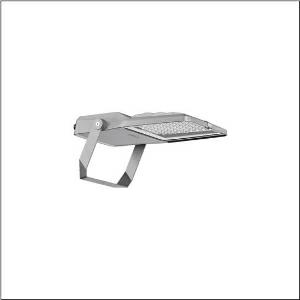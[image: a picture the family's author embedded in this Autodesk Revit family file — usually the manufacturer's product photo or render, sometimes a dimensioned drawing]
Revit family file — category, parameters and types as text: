
# Revit family: floodlight_fl_21_iq_mini___pl43_5xa7772d3a1a_c631
name_source: partatom
category: Lighting Fixtures
units: mm (PartAtom-declared; Revit-internal decimal feet)

## family parameters
Cut with Voids When Loaded = No
Host = Face
Light Source = No
Part Type = Normal
Room Calculation Point = No
Round Connector Dimension = Use Diameter
Shared = No

## types (1)
- --- (1 x LED, 15730 lm, 143 W, 3000K)
    Apparent Load = 143 VA
    CIE Flux Codes = 27 78 99 100 100
    Color Rendering = 80
    Color Temperature = 3000K
    Default Elevation = 1800 mm
    Description = Floodlight FL 21 iQ mini, floodlight, primary light control with lens, of PMMA, primary optical cover: protective disc, of toughened safety glass, transparent, light distribution: PL43, light emission: direct distribution, installation type: surface-mounted, LED, High Power LED, rated luminous flux: 15.730lm, luminous efficacy: 110lm/W, light colour: 830, colour temperature: 3000K, control gear: iQ Street-Remote/DALI, control: Street-Remote, Auto-Match, Temp-Guard, Night-Set, Smart-Wire, Desk-Remote (wireless, voltage-free reading and setting of iQ features in the workshop via application-optimized NFC function/RFID function), optimised constant luminous flux control (CLO 2.0), with terminal, 6-pole, mains connection: 220..240V, AC, 50/60Hz, start of lifetime: 143W, end of service life: 152W, reduction: 61W, luminaire housing, of diecast aluminium, powder-coated, Siteco® metallic grey (DB 702S), corrosivity category C5 mid according to DIN EN ISO 12944, suitable for swimming pools, chlorine-resistant, sealing non-destructively replaceable, mounting bracket, of steel, galvanised, powder-coated, Siteco® metallic grey (DB 702S), protection rating (complete): IP66, insulation class (complete): insulation class II (safety insulation), certification: CE, ENEC, VDE, protection symbol: D, impact resistance: IK08, permissible operating ambient temperature: -40..+40°C, permissible operating ambient temperature for outdoor applications: -40..+50°C, standard: DIN EN 12944, LABS conformity tested according to VDMA 24364:2018-05, packaging unit: 1 piece

Light Distribution: PL43
    Height = 70 mm
    Lamp = 1 x LED
    Lamp Light Flux = 15730 lm
    Lamp Power = 143 W
    Lamp count = 1
    Length = 485 mm
    Luminous efficacy = 110 lm/W
    Manufacturer = Siteco
    ModVariant = No
    Model = 5XA7772D3A1A
    Number of Poles = 1
    OnlyDefault = Yes
    Power Factor = 1
    Product Name = Floodlight FL 21 iQ mini | PL43
    Product group = floodlight | pylon annexe
    ProductGroupID = 6200
    Protection Class = Protection class II
    Protection Degree = IP 66
    RLX_Detail_Level = 1
    RLX_Emergency_Light_Flux = 0 lm
    RLX_Emergency_Type = 0
    RLX_Emergency_Type_DB = No
    RlxData = <blob elided: 96505 chars, md5=b7f6127f>
    Socket = socket
    Standby Power = 0 W
    System Light Flux = 15730 lm
    System Power = 143 W
    Type Comments = factory setting: luminous flux: 100 % | dim-lin: 254 | 730 mA
    Type Image = l_1006845.jpg
    URL = http://relux.com
    VarID = @adj_161586
    Voltage = 0 V
    Weight = 0.00 kg
    Width = 337 mm

## geometry (parser evidence)
native form markers: Blend x4, Sweep x12
no freeform markers — native parametric forms only
